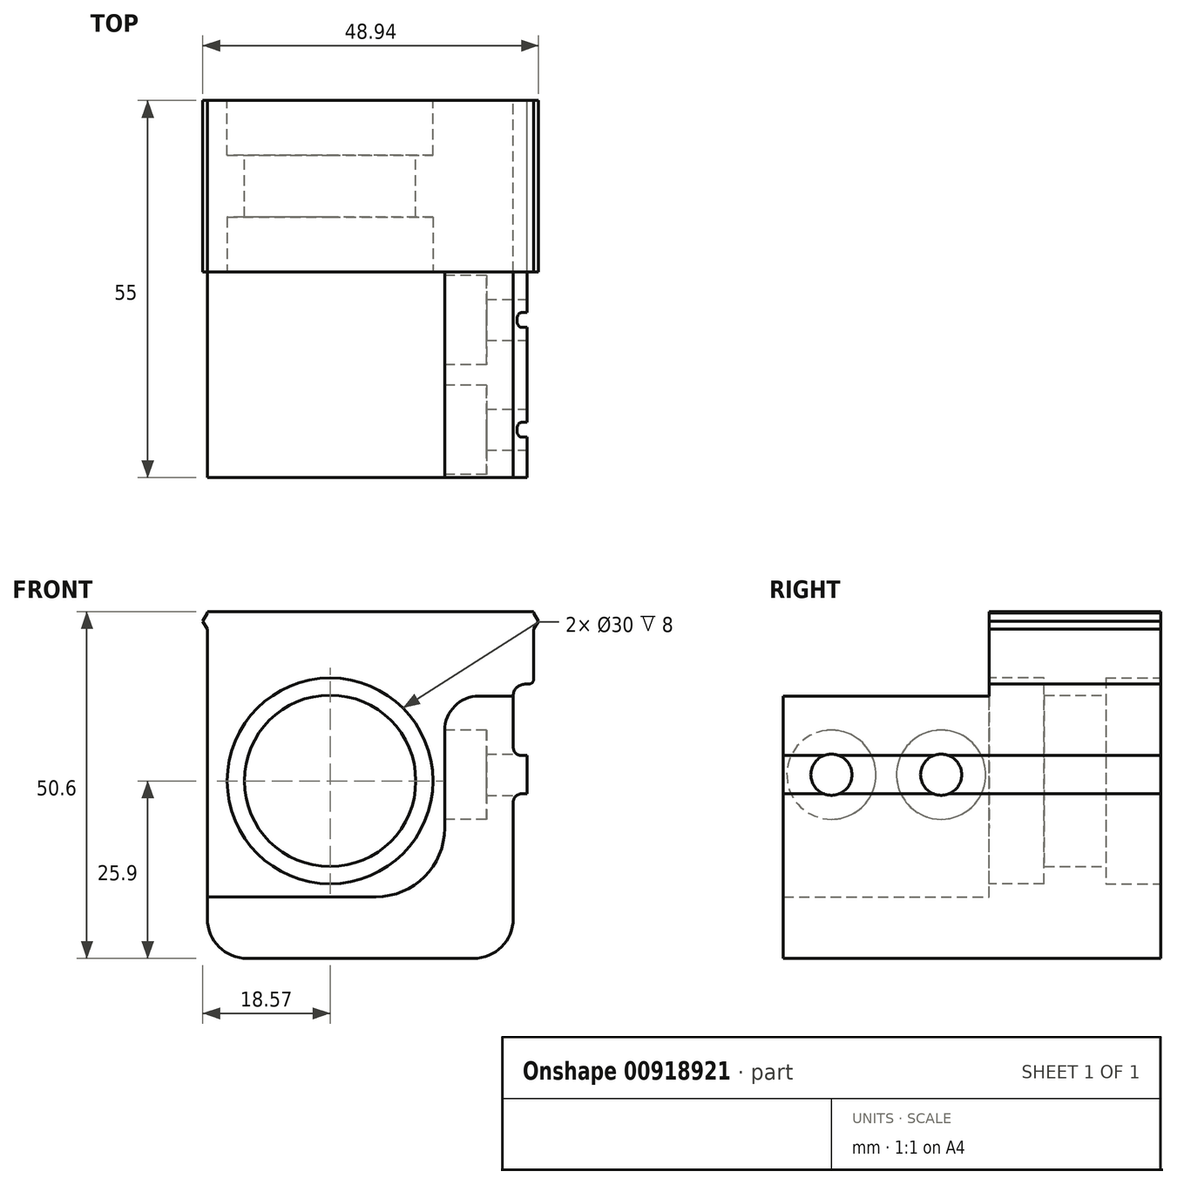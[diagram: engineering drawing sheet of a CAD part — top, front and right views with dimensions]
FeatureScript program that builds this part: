
annotation { "Feature Type Name" : "Feature", "Feature Type Description" : "" }
export const myFeature = defineFeature(function(context is Context, id is Id, definition is map)
    precondition{}
    {
        {
            var Q0;
            Q0=qCreatedBy(makeId("Front.planeOp"),FACE);
            var sketch = newSketch(context, id + "F0", { "sketchPlane" : qUnion([Q0])});
            skLineSegment(sketch, "E0.0", {"start": v(-23.7, 23.56) * mm, "end": v(-23.7, 23.8) * mm});
            skLineSegment(sketch, "E0.1", {"start": v(-24.37, 22.4) * mm, "end": v(-23.7, 23.56) * mm});
            skLineSegment(sketch, "E0.2", {"start": v(-23.7, 21.24) * mm, "end": v(-24.37, 22.4) * mm});
            skLineSegment(sketch, "E0.3", {"start": v(-23.7, -21) * mm, "end": v(-23.7, 21.24) * mm});
            skArc(sketch, "E0.4", {"start": v(-23.7, -21) * mm, "mid": v(-22, -25.1) * mm, "end": v(-17.9, -26.8) * mm});
            skLineSegment(sketch, "E0.5", {"start": v(-23.7, 23.8) * mm, "end": v(23.9, 23.8) * mm});
            skLineSegment(sketch, "E0.6", {"start": v(15.1, -26.8) * mm, "end": v(-17.9, -26.8) * mm});
            skArc(sketch, "E0.7", {"start": v(15.1, -26.8) * mm, "mid": v(19.2, -25.1) * mm, "end": v(20.9, -21) * mm});
            skLineSegment(sketch, "E0.8", {"start": v(20.9, -4) * mm, "end": v(20.9, -21) * mm});
            skArc(sketch, "E0.9", {"start": v(22.1, -2.8) * mm, "mid": v(21.25, -3.15) * mm, "end": v(20.9, -4) * mm});
            skLineSegment(sketch, "E0.10", {"start": v(22.9, -2.8) * mm, "end": v(22.1, -2.8) * mm});
            skLineSegment(sketch, "E0.11", {"start": v(22.9, -2.8) * mm, "end": v(22.9, 2.8) * mm});
            skLineSegment(sketch, "E0.12", {"start": v(23.9, 21.24) * mm, "end": v(23.9, 14) * mm});
            skLineSegment(sketch, "E0.13", {"start": v(24.57, 22.4) * mm, "end": v(23.9, 21.24) * mm});
            skLineSegment(sketch, "E0.14", {"start": v(23.9, 23.56) * mm, "end": v(24.57, 22.4) * mm});
            skLineSegment(sketch, "E0.15", {"start": v(23.9, 23.8) * mm, "end": v(23.9, 23.56) * mm});
            skArc(sketch, "E0.16", {"start": v(23.1, 13.2) * mm, "mid": v(23.67, 13.43) * mm, "end": v(23.9, 14) * mm});
            skLineSegment(sketch, "E0.17", {"start": v(23.1, 13.2) * mm, "end": v(22.6, 13.2) * mm});
            skArc(sketch, "E0.18", {"start": v(22.6, 13.2) * mm, "mid": v(21.4, 12.7) * mm, "end": v(20.9, 11.5) * mm});
            skLineSegment(sketch, "E0.19", {"start": v(20.9, 11.5) * mm, "end": v(20.9, 4) * mm});
            skArc(sketch, "E0.20", {"start": v(20.9, 4) * mm, "mid": v(21.25, 3.15) * mm, "end": v(22.1, 2.8) * mm});
            skLineSegment(sketch, "E0.21", {"start": v(22.1, 2.8) * mm, "end": v(22.9, 2.8) * mm});
            skSolve(sketch);
        }
        {
            var Q0;
            Q0=qSketchRegion(id+"F0",true);
            extrude(context, id + "F1", {"entities" : qUnion([Q0]), "depth" : 55 * mm, "offsetDistance" : 25 * mm});
        }
        {
            var Q0;
            Q0=makeQuery(id+"F1.opExtrude","CAP_FACE",FACE,{"disambiguationData":[OSD([sQuery(id+"F0.wireOp",EDGE,"E0.0"),sQuery(id+"F0.wireOp",EDGE,"E0.1"),sQuery(id+"F0.wireOp",EDGE,"E0.2"),sQuery(id+"F0.wireOp",EDGE,"E0.3"),sQuery(id+"F0.wireOp",EDGE,"E0.4"),sQuery(id+"F0.wireOp",EDGE,"E0.5"),sQuery(id+"F0.wireOp",EDGE,"E0.6"),sQuery(id+"F0.wireOp",EDGE,"E0.7"),sQuery(id+"F0.wireOp",EDGE,"E0.8"),sQuery(id+"F0.wireOp",EDGE,"E0.9"),sQuery(id+"F0.wireOp",EDGE,"E0.10"),sQuery(id+"F0.wireOp",EDGE,"E0.11"),sQuery(id+"F0.wireOp",EDGE,"E0.12"),sQuery(id+"F0.wireOp",EDGE,"E0.13"),sQuery(id+"F0.wireOp",EDGE,"E0.14"),sQuery(id+"F0.wireOp",EDGE,"E0.15"),sQuery(id+"F0.wireOp",EDGE,"E0.16"),sQuery(id+"F0.wireOp",EDGE,"E0.17"),sQuery(id+"F0.wireOp",EDGE,"E0.18"),sQuery(id+"F0.wireOp",EDGE,"E0.19"),sQuery(id+"F0.wireOp",EDGE,"E0.20"),sQuery(id+"F0.wireOp",EDGE,"E0.21")])],"isStart":false});
            var sketch = newSketch(context, id + "F2", { "sketchPlane" : qUnion([Q0])});
            skLineSegment(sketch, "E1", {"start": v(26.68, 11.46) * mm, "end": v(15.9, 11.46) * mm});
            skLineSegment(sketch, "E2", {"start": v(10.9, 6.46) * mm, "end": v(10.9, -11.8) * mm});
            skLineSegment(sketch, "E3", {"start": v(5.9, -17.8) * mm, "end": v(-26.83, -17.8) * mm});
            skLineSegment(sketch, "E4", {"start": v(-26.83, -17.8) * mm, "end": v(-26.83, 26.7) * mm});
            skLineSegment(sketch, "E5", {"start": v(-26.83, 26.7) * mm, "end": v(26.68, 26.7) * mm});
            skLineSegment(sketch, "E6", {"start": v(26.68, 26.7) * mm, "end": v(26.68, 11.46) * mm});
            skPoint(sketch, "E7.visualSharp", {"position": v(10.9, -17.8) * mm});
            skPoint(sketch, "E8.visualSharp", {"position": v(10.9, 11.46) * mm});
            skArc(sketch, "E8.filletArc", {"start": v(15.9, 11.46) * mm, "mid": v(12.36, 10) * mm, "end": v(10.9, 6.46) * mm});
            skLineSegment(sketch, "E9", {"start": v(5.9, -17.8) * mm, "end": v(10.9, -17.8) * mm});
            skLineSegment(sketch, "E10", {"start": v(10.9, -11.8) * mm, "end": v(10.9, -17.8) * mm});
            skSolve(sketch);
        }
        {
            var Q0;
            Q0=qSketchRegion(id+"F2",true);
            extrude(context, id + "F3", {"entities" : qUnion([Q0]), "operationType" : NewBodyOperationType.REMOVE, "oppositeDirection" : true, "depth" : 30 * mm, "offsetDistance" : 25 * mm});
        }
        {
            var Q0;
            Q0=makeQuery(id+"F1.opExtrude","SWEPT_FACE",FACE,{"disambiguationData":[OSD([sQuery(id+"F0.wireOp",EDGE,"E0.11")])]});
            var sketch = newSketch(context, id + "F4", { "sketchPlane" : qUnion([Q0])});
            skCircle(sketch, "E11", {"center": v(-48, 0) * mm, "radius": 3 * mm});
            skCircle(sketch, "E12", {"center": v(-32, 0) * mm, "radius": 3 * mm});
            skSolve(sketch);
        }
        {
            var Q0;
            Q0=qSketchRegion(id+"F4",true);
            extrude(context, id + "F5", {"entities" : qUnion([Q0]), "operationType" : NewBodyOperationType.REMOVE, "oppositeDirection" : true, "depth" : 25 * mm, "offsetDistance" : 25 * mm});
        }
        {
            var Q0;
            Q0=makeQuery(id+"F1.opExtrude","CAP_FACE",FACE,{"disambiguationData":[OSD([sQuery(id+"F0.wireOp",EDGE,"E0.0"),sQuery(id+"F0.wireOp",EDGE,"E0.1"),sQuery(id+"F0.wireOp",EDGE,"E0.2"),sQuery(id+"F0.wireOp",EDGE,"E0.3"),sQuery(id+"F0.wireOp",EDGE,"E0.4"),sQuery(id+"F0.wireOp",EDGE,"E0.5"),sQuery(id+"F0.wireOp",EDGE,"E0.6"),sQuery(id+"F0.wireOp",EDGE,"E0.7"),sQuery(id+"F0.wireOp",EDGE,"E0.8"),sQuery(id+"F0.wireOp",EDGE,"E0.9"),sQuery(id+"F0.wireOp",EDGE,"E0.10"),sQuery(id+"F0.wireOp",EDGE,"E0.11"),sQuery(id+"F0.wireOp",EDGE,"E0.12"),sQuery(id+"F0.wireOp",EDGE,"E0.13"),sQuery(id+"F0.wireOp",EDGE,"E0.14"),sQuery(id+"F0.wireOp",EDGE,"E0.15"),sQuery(id+"F0.wireOp",EDGE,"E0.16"),sQuery(id+"F0.wireOp",EDGE,"E0.17"),sQuery(id+"F0.wireOp",EDGE,"E0.18"),sQuery(id+"F0.wireOp",EDGE,"E0.19"),sQuery(id+"F0.wireOp",EDGE,"E0.20"),sQuery(id+"F0.wireOp",EDGE,"E0.21")])],"isStart":true});
            var sketch = newSketch(context, id + "F6", { "sketchPlane" : qUnion([Q0])});
            skCircle(sketch, "E13", {"center": v(5.8, -0.9) * mm, "radius": 12.5 * mm});
            skLineSegment(sketch, "E14.bottom", {"start": v(-10.7, 22.1) * mm, "end": v(22.3, 22.1) * mm, "construction": true});
            skLineSegment(sketch, "E14.top", {"start": v(-10.7, -23.9) * mm, "end": v(22.3, -23.9) * mm, "construction": true});
            skLineSegment(sketch, "E14.left", {"start": v(-10.7, 22.1) * mm, "end": v(-10.7, -23.9) * mm, "construction": true});
            skLineSegment(sketch, "E14.right", {"start": v(22.3, 22.1) * mm, "end": v(22.3, -23.9) * mm, "construction": true});
            skSolve(sketch);
        }
        {
            var Q0;
            Q0=qSketchRegion(id+"F6",true);
            extrude(context, id + "F7", {"entities" : qUnion([Q0]), "operationType" : NewBodyOperationType.REMOVE, "endBound" : BoundingType.UP_TO_NEXT, "oppositeDirection" : true, "depth" : 25 * mm, "offsetDistance" : 25 * mm});
        }
        {
            var Q0;
            Q0=makeQuery(id+"F1.opExtrude","CAP_FACE",FACE,{"disambiguationData":[OSD([sQuery(id+"F0.wireOp",EDGE,"E0.0"),sQuery(id+"F0.wireOp",EDGE,"E0.1"),sQuery(id+"F0.wireOp",EDGE,"E0.2"),sQuery(id+"F0.wireOp",EDGE,"E0.3"),sQuery(id+"F0.wireOp",EDGE,"E0.4"),sQuery(id+"F0.wireOp",EDGE,"E0.5"),sQuery(id+"F0.wireOp",EDGE,"E0.6"),sQuery(id+"F0.wireOp",EDGE,"E0.7"),sQuery(id+"F0.wireOp",EDGE,"E0.8"),sQuery(id+"F0.wireOp",EDGE,"E0.9"),sQuery(id+"F0.wireOp",EDGE,"E0.10"),sQuery(id+"F0.wireOp",EDGE,"E0.11"),sQuery(id+"F0.wireOp",EDGE,"E0.12"),sQuery(id+"F0.wireOp",EDGE,"E0.13"),sQuery(id+"F0.wireOp",EDGE,"E0.14"),sQuery(id+"F0.wireOp",EDGE,"E0.15"),sQuery(id+"F0.wireOp",EDGE,"E0.16"),sQuery(id+"F0.wireOp",EDGE,"E0.17"),sQuery(id+"F0.wireOp",EDGE,"E0.18"),sQuery(id+"F0.wireOp",EDGE,"E0.19"),sQuery(id+"F0.wireOp",EDGE,"E0.20"),sQuery(id+"F0.wireOp",EDGE,"E0.21")])],"isStart":false});
            var sketch = newSketch(context, id + "F8", { "sketchPlane" : qUnion([Q0])});
            skCircle(sketch, "E15", {"center": v(-5.8, -0.9) * mm, "radius": 15 * mm});
            skSolve(sketch);
        }
        {
            var Q0;
            Q0=qSketchRegion(id+"F8",true);
            extrude(context, id + "F9", {"entities" : qUnion([Q0]), "operationType" : NewBodyOperationType.REMOVE, "oppositeDirection" : true, "depth" : 38 * mm, "offsetDistance" : 25 * mm});
        }
        {
            var Q0;
            Q0=makeQuery(id+"F1.opExtrude","CAP_FACE",FACE,{"disambiguationData":[OSD([sQuery(id+"F0.wireOp",EDGE,"E0.0"),sQuery(id+"F0.wireOp",EDGE,"E0.1"),sQuery(id+"F0.wireOp",EDGE,"E0.2"),sQuery(id+"F0.wireOp",EDGE,"E0.3"),sQuery(id+"F0.wireOp",EDGE,"E0.4"),sQuery(id+"F0.wireOp",EDGE,"E0.5"),sQuery(id+"F0.wireOp",EDGE,"E0.6"),sQuery(id+"F0.wireOp",EDGE,"E0.7"),sQuery(id+"F0.wireOp",EDGE,"E0.8"),sQuery(id+"F0.wireOp",EDGE,"E0.9"),sQuery(id+"F0.wireOp",EDGE,"E0.10"),sQuery(id+"F0.wireOp",EDGE,"E0.11"),sQuery(id+"F0.wireOp",EDGE,"E0.12"),sQuery(id+"F0.wireOp",EDGE,"E0.13"),sQuery(id+"F0.wireOp",EDGE,"E0.14"),sQuery(id+"F0.wireOp",EDGE,"E0.15"),sQuery(id+"F0.wireOp",EDGE,"E0.16"),sQuery(id+"F0.wireOp",EDGE,"E0.17"),sQuery(id+"F0.wireOp",EDGE,"E0.18"),sQuery(id+"F0.wireOp",EDGE,"E0.19"),sQuery(id+"F0.wireOp",EDGE,"E0.20"),sQuery(id+"F0.wireOp",EDGE,"E0.21")])],"isStart":true});
            var sketch = newSketch(context, id + "F10", { "sketchPlane" : qUnion([Q0])});
            skCircle(sketch, "E16", {"center": v(5.8, -0.9) * mm, "radius": 15 * mm});
            skSolve(sketch);
        }
        {
            var Q0;
            Q0=qSketchRegion(id+"F10",true);
            extrude(context, id + "F11", {"entities" : qUnion([Q0]), "operationType" : NewBodyOperationType.REMOVE, "oppositeDirection" : true, "depth" : 8 * mm, "offsetDistance" : 25 * mm});
        }
        {
            var Q0;
            Q0=qCreatedBy(makeId("Right.planeOp"),FACE);
            var sketch = newSketch(context, id + "F12", { "sketchPlane" : qUnion([Q0])});
            skCircle(sketch, "E17", {"center": v(-32, 0) * mm, "radius": 6.5 * mm});
            skCircle(sketch, "E18", {"center": v(-48, 0) * mm, "radius": 6.5 * mm});
            skSolve(sketch);
        }
        {
            var Q0;
            Q0=qSketchRegion(id+"F12",true);
            extrude(context, id + "F13", {"entities" : qUnion([Q0]), "operationType" : NewBodyOperationType.REMOVE, "depth" : 17 * mm, "offsetDistance" : 25 * mm});
        }
        {
            var Q0;
            Q0=makeQuery(id+"F3.boolean.opBoolean","COPY",EDGE,{"derivedFrom":makeQuery(id+"F3.opExtrude","SWEPT_EDGE",EDGE,{"disambiguationData":[OSD([sQuery(id+"F2.wireOp",EDGE,"E9"),sQuery(id+"F2.wireOp",EDGE,"E10")])]})});
            fillet(context, id + "F14", {"entities" : qUnion([Q0]), "radius" : 10 * mm, "tangentPropagation" : true, "allowEdgeOverflow" : false});
        }
    });
